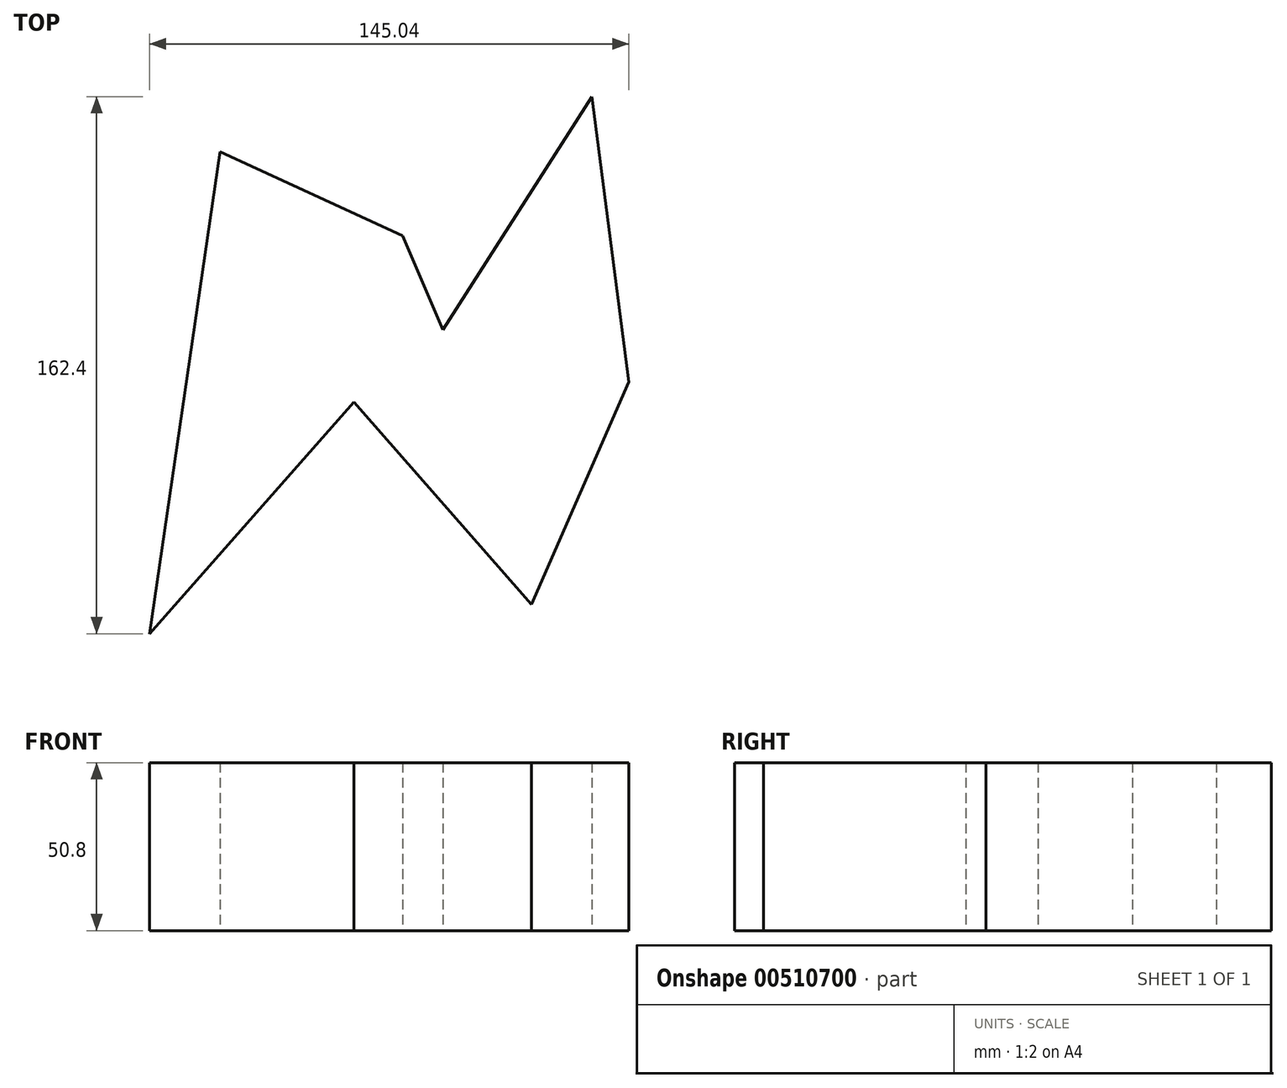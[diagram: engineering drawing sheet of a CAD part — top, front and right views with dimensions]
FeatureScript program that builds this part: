
annotation { "Feature Type Name" : "Feature", "Feature Type Description" : "" }
export const myFeature = defineFeature(function(context is Context, id is Id, definition is map)
    precondition{}
    {
        {
            var Q0;
            Q0=qCreatedBy(makeId("Top.planeOp"),FACE);
            var sketch = newSketch(context, id + "F0", { "sketchPlane" : qUnion([Q0])});
            skLineSegment(sketch, "E0", {"start": v(-67.42, 69.5) * mm, "end": v(-88.78, -76.3) * mm});
            skLineSegment(sketch, "E1", {"start": v(-88.78, -76.3) * mm, "end": v(-26.74, -6.11) * mm});
            skLineSegment(sketch, "E2", {"start": v(-27.08, -6.11) * mm, "end": v(26.83, -67.48) * mm});
            skLineSegment(sketch, "E3", {"start": v(26.83, -67.48) * mm, "end": v(56.33, 0) * mm});
            skLineSegment(sketch, "E4", {"start": v(56.33, -0.69) * mm, "end": v(45.14, 86.1) * mm});
            skLineSegment(sketch, "E5", {"start": v(45.14, 86.1) * mm, "end": v(0, 15.59) * mm});
            skLineSegment(sketch, "E6", {"start": v(0, 15.59) * mm, "end": v(-12.16, 44.07) * mm});
            skLineSegment(sketch, "E7", {"start": v(-12.16, 44.07) * mm, "end": v(-67.42, 69.5) * mm});
            skSolve(sketch);
        }
        {
            var Q0;
            {var subQ7=sQuery(id+"F0.wireOp",EDGE,"E0");Q0=makeQuery(id+"F0.imprint","IMPRINT",FACE,{"disambiguationData":[TD([[makeQuery(id+"F0.imprint","IMPRINT",EDGE,{"derivedFrom":subQ7}),1.0]])]});}
            extrude(context, id + "F1", {"entities" : qUnion([Q0]), "depth" : 50.8 * mm});
        }
    });
